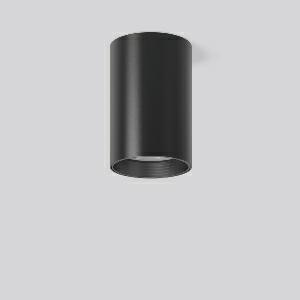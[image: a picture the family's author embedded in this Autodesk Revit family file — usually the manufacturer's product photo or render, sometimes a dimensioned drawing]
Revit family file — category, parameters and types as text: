
# Revit family: heledon_maxi_a_931221_003_1_335d
name_source: partatom
category: Lighting Fixtures
units: mm (PartAtom-declared; Revit-internal decimal feet)

## family parameters
Cut with Voids When Loaded = No
Host = Face
Light Source = No
Part Type = Normal
Room Calculation Point = No
Round Connector Dimension = Use Diameter
Shared = No

## types (1)
- HELEDON maxi A (1 x LED Modul 940, 2850 lm, 4000)
    Apparent Load = 25 VA
    Approval mark = CE
    CIE Flux Codes = 96 100 100 100 100
    Color Rendering = 92
    Color Temperature = 4000
    Default Elevation = 1800 mm
    Description = Series: HELEDON maxi
Cylindrical surface-mounted downlight. Housing: die-cast aluminium, powder-coated. Internal ceiling frame polycarbonate with bayonet mounting. Black plastic ring and recessed LED to prevent glare from the side. Optical assembly with lens made of plastic (polycarbonate) for the best homogeneous light distribution - can be changed without tools. Best colour rendering index Ra>90. Suitable for Ceiling mounting. Easy installation with a separate ceiling frame with bayonet mounting and plug connection. Driver integrated. Connected via plug-in connector. High quality converter without flickering and stroboscopic effect. The following accessories can be mounted without use of tools: interchangeable lenses, decorative glasses, honeycomb louvre, clear and frosted diffusers, white interchangeable plastic ring. 
Colour: deep black, matt (RAL 9005)
Diameter: 123 mm
Height: 183 mm
Lamp: LED
Socket: without socket
Colour temperature: 4000K
Colour rendering index (CRI): 92
System power: 25 W
Rated luminous flux: 2850 lm
Luminous efficiency: 114 lm/W
Control gear: Regulated power supply
Protection class: I
Type of protection: IP 20
    Height = 183 mm
    Lamp = 1 x LED Modul 940
    Lamp Light Flux = 2850 lm
    Lamp count = 1
    Length = 123 mm
    Lifetime = 50000 h
    Luminous efficacy = 114 lm/W
    Manufacturer = RZB
    ModVariant = No
    Model = 931221.003.1
    Mounting Place = Ceiling
    Mounting Type = Surface mounted
    Number of Poles = 1
    OnlyDefault = Yes
    Power Factor = 1
    Product Name = HELEDON maxi A
    Product group = Surface mounted downlights
    ProductGroupID = 302
    Protection Class = Protection class I
    Protection Degree = IP 20
    RLX_Detail_Level = 1
    RLX_Emergency_Light_Flux = 0 lm
    RLX_Emergency_Type = 0
    RLX_Emergency_Type_DB = No
    RlxData = <blob elided: 97677 chars, md5=b34aef15>
    Socket = socket
    Standby Power = 0 W
    System Light Flux = 2850 lm
    System Power = 25 W
    Type Comments = Product without accessories
    Type Image = 931193.003.jpg
    URL = http://relux.com
    VarID = ---
    Voltage = 230 V
    Voltage Range = 220-240 V
    Weight = 0.00 kg
    Width = 0 mm  [stored 0 ft]

note: [stored X ft] marks values corroborated as IEEE doubles in the binary element streams (Revit-internal decimal feet)

## geometry (parser evidence)
native form markers: Blend x4, Sweep x12
no freeform markers — native parametric forms only
